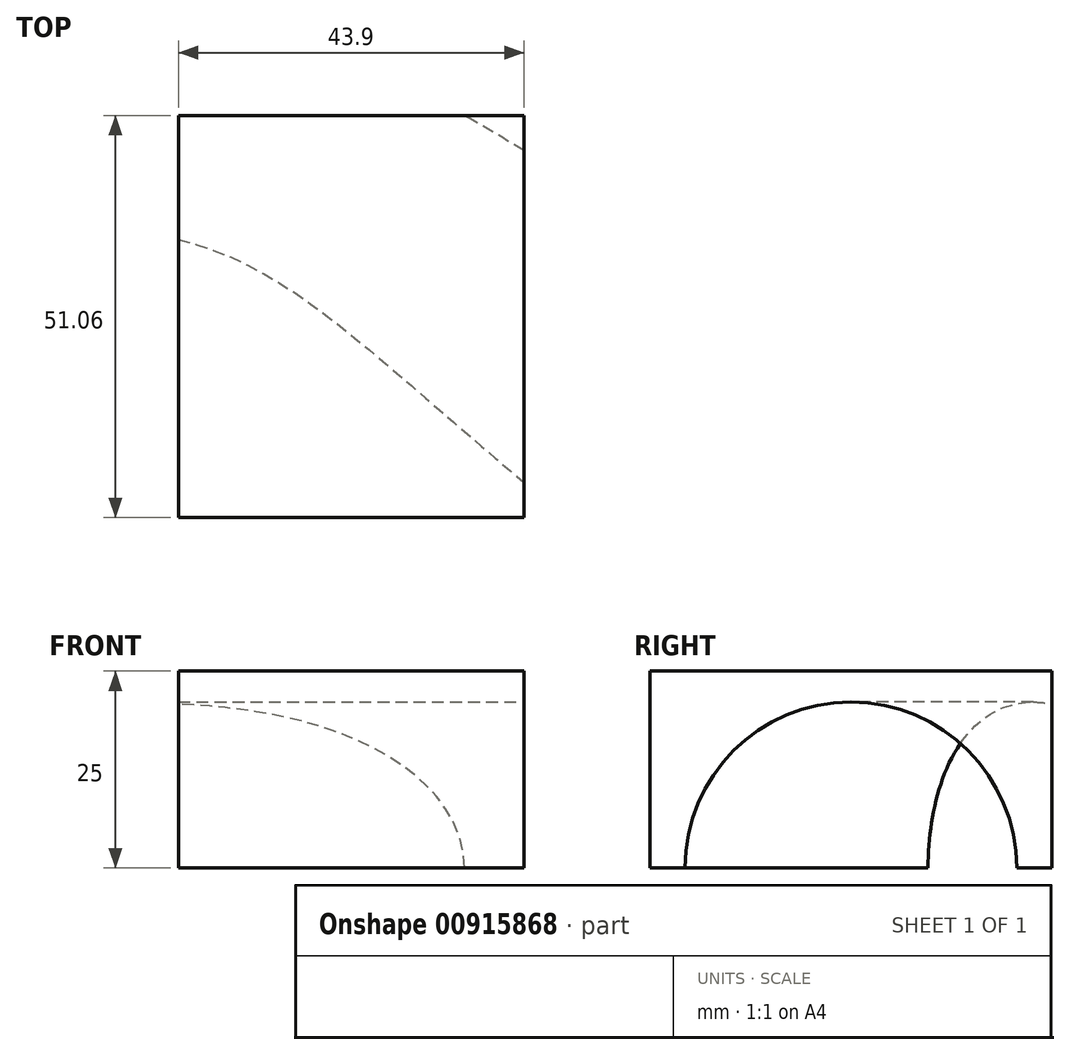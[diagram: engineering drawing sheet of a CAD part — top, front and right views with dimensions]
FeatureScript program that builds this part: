
annotation { "Feature Type Name" : "Feature", "Feature Type Description" : "" }
export const myFeature = defineFeature(function(context is Context, id is Id, definition is map)
    precondition{}
    {
        {
            var Q0;
            Q0=qCreatedBy(makeId("Top.planeOp"),FACE);
            var sketch = newSketch(context, id + "F0", { "sketchPlane" : qUnion([Q0])});
            skLineSegment(sketch, "E0.bottom", {"start": v(21.95, -25.53) * mm, "end": v(-21.95, -25.53) * mm});
            skLineSegment(sketch, "E0.top", {"start": v(21.95, 25.53) * mm, "end": v(-21.95, 25.53) * mm});
            skLineSegment(sketch, "E0.left", {"start": v(21.95, -25.53) * mm, "end": v(21.95, 25.53) * mm});
            skLineSegment(sketch, "E0.right", {"start": v(-21.95, -25.53) * mm, "end": v(-21.95, 25.53) * mm});
            skPoint(sketch, "E0.middle", {"position": v(0, 0) * mm});
            skSolve(sketch);
        }
        {
            var Q0;
            Q0=makeQuery(id+"F0.imprint","IMPRINT",FACE,{"disambiguationData":[TD([[makeQuery(id+"F0.imprint","IMPRINT",EDGE,{"derivedFrom":sQuery(id+"F0.wireOp",EDGE,"E0.bottom")}),-1.0]])]});
            extrude(context, id + "F1", {"entities" : qUnion([Q0]), "depth" : 25 * mm, "offsetDistance" : 25 * mm});
        }
        {
            var Q0;
            Q0=makeQuery(id+"F1.opExtrude","SWEPT_FACE",FACE,{"disambiguationData":[OSD([sQuery(id+"F0.wireOp",EDGE,"E0.left")])]});
            var sketch = newSketch(context, id + "F2", { "sketchPlane" : qUnion([Q0])});
            skCircle(sketch, "E1", {"center": v(0, 13.52) * mm, "radius": 3.69 * mm});
            skCircle(sketch, "E2", {"center": v(0, 0) * mm, "radius": 21.06 * mm});
            skSolve(sketch);
        }
        {
            var Q0;
            Q0=qCreatedBy(makeId("Top.planeOp"),FACE);
            var sketch = newSketch(context, id + "F3", { "sketchPlane" : qUnion([Q0])});
            skFitSpline(sketch, "E3", {"points": [v(0, 0) * mm, v(-73.87, 0) * mm], "startDerivative": vector(-82.2, 45.61) * mm, "endDerivative": vector(-77.46, -47.34) * mm});
            skSolve(sketch);
        }
        {
            var Q0;
            {var subQ0=sQuery(id+"F2.wireOp",EDGE,"E2");var subQ1=makeQuery(id+"F1.opExtrude","CAP_EDGE",EDGE,{"disambiguationData":[OSD([sQuery(id+"F0.wireOp",EDGE,"E0.left")])],"isStart":true});var subQ2=makeQuery(id+"F2.imprint","INTERSECT",VERTEX,{"disambiguationData":[OD(0.0)],"derivedFrom":[subQ1,subQ0]});Q0=makeQuery(id+"F2.imprint","IMPRINT",FACE,{"disambiguationData":[TD([[makeQuery(id+"F2.imprint","IMPRINT",EDGE,{"disambiguationData":[TD([[subQ2,-1.0]])],"derivedFrom":subQ0}),1.0]])]});}
            var Q1;
            Q1=makeQuery(id+"F2.imprint","IMPRINT",FACE,{"disambiguationData":[TD([[makeQuery(id+"F2.imprint","IMPRINT",EDGE,{"derivedFrom":sQuery(id+"F2.wireOp",EDGE,"E1")}),-1.0]])]});
            var Q2;
            Q2=makeQuery(id+"F2.imprint","IMPRINT",FACE,{"disambiguationData":[TD([[makeQuery(id+"F2.imprint","IMPRINT",EDGE,{"derivedFrom":sQuery(id+"F2.wireOp",EDGE,"E1")}),1.0]])]});
            var Q3;
            Q3=sQuery(id+"F3.wireOp",EDGE,"E3");
            sweep(context, id + "F4", {"operationType" : NewBodyOperationType.REMOVE, "profiles" : qUnion([Q0, Q1, Q2]), "path" : qUnion([Q3])});
        }
    });
